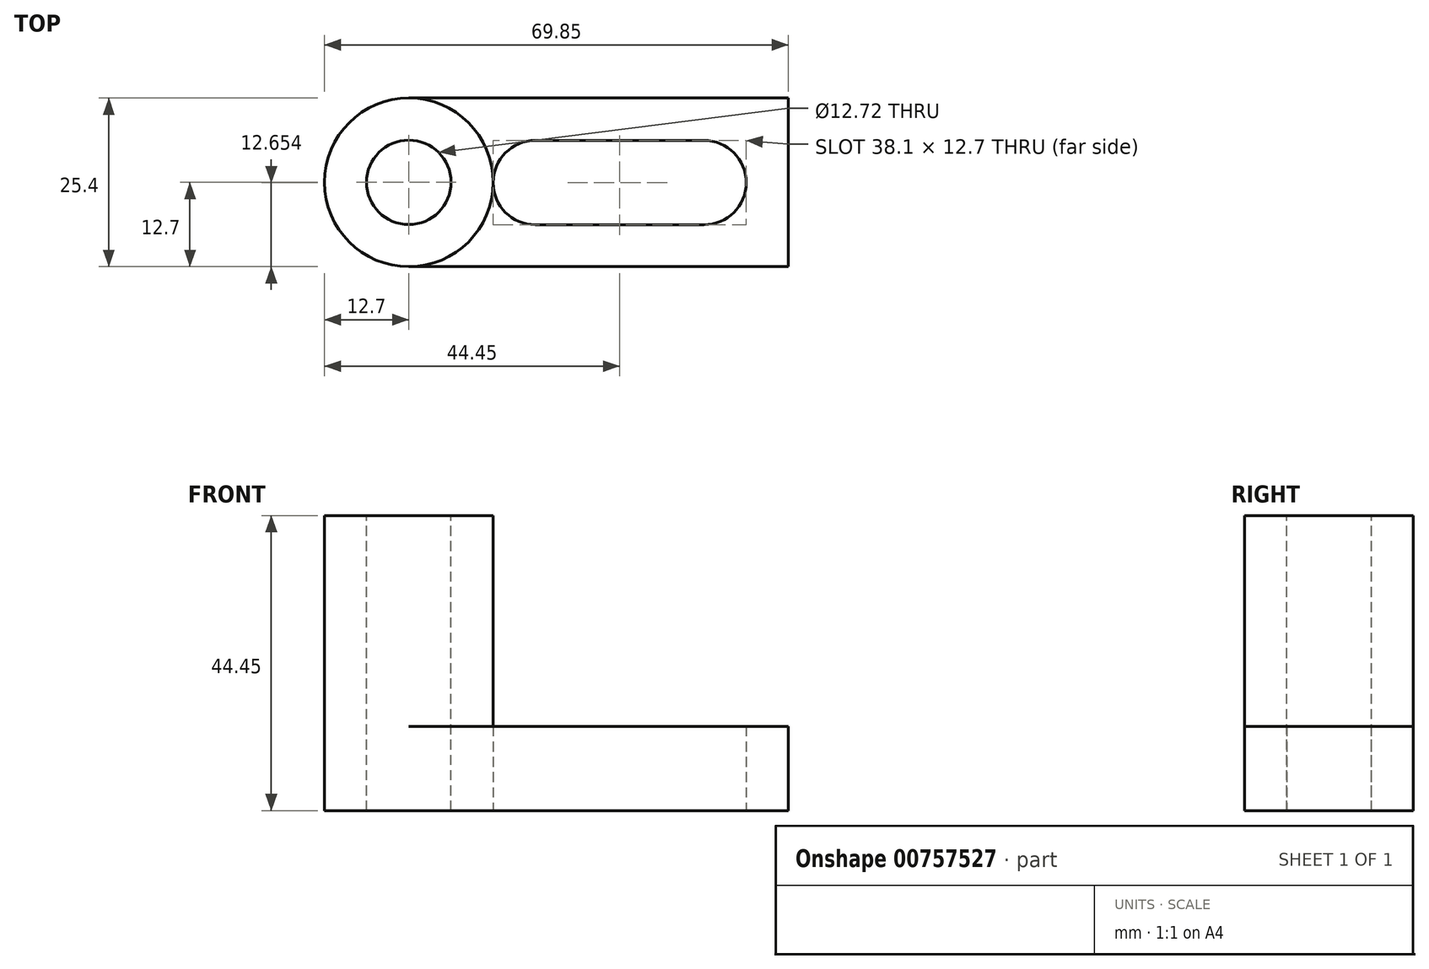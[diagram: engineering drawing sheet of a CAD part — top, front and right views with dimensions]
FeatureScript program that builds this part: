
annotation { "Feature Type Name" : "Feature", "Feature Type Description" : "" }
export const myFeature = defineFeature(function(context is Context, id is Id, definition is map)
    precondition{}
    {
        {
            var Q0;
            Q0=qCreatedBy(makeId("Front.planeOp"),FACE);
            var sketch = newSketch(context, id + "F0", { "sketchPlane" : qUnion([Q0])});
            skLineSegment(sketch, "E0", {"start": v(0, 0) * mm, "end": v(-69.85, 0) * mm});
            skLineSegment(sketch, "E1", {"start": v(-69.85, 0) * mm, "end": v(-69.85, 44.45) * mm});
            skLineSegment(sketch, "E2", {"start": v(-69.85, 44.45) * mm, "end": v(0, 44.45) * mm});
            skLineSegment(sketch, "E3", {"start": v(0, 44.45) * mm, "end": v(0, 0) * mm});
            skSolve(sketch);
        }
        {
            var Q0;
            Q0 = qSketchRegion(id + "F0", true);
            extrude(context, id + "F1", {"entities" : qUnion([Q0]), "depth" : 25.4 * mm, "offsetDistance" : 25.4 * mm});
        }
        {
            var Q0;
            Q0=makeQuery(id+"F1.opExtrude","CAP_FACE",FACE,{"disambiguationData":[OSD([sQuery(id+"F0.wireOp",EDGE,"E0"),sQuery(id+"F0.wireOp",EDGE,"E1"),sQuery(id+"F0.wireOp",EDGE,"E2"),sQuery(id+"F0.wireOp",EDGE,"E3")])],"isStart":false});
            var sketch = newSketch(context, id + "F2", { "sketchPlane" : qUnion([Q0])});
            skLineSegment(sketch, "E4", {"start": v(-44.45, 44.45) * mm, "end": v(-44.45, 12.7) * mm});
            skLineSegment(sketch, "E5", {"start": v(-44.45, 12.7) * mm, "end": v(0, 12.7) * mm});
            skSolve(sketch);
        }
        {
            var Q0;
            {var subQ0=sQuery(id+"F2.wireOp",EDGE,"E4");Q0=makeQuery(id+"F2.imprint","IMPRINT",FACE,{"disambiguationData":[TD([[makeQuery(id+"F2.imprint","IMPRINT",EDGE,{"derivedFrom":subQ0}),1.0]])]});}
            extrude(context, id + "F3", {"entities" : qUnion([Q0]), "operationType" : NewBodyOperationType.REMOVE, "endBound" : BoundingType.THROUGH_ALL, "oppositeDirection" : true, "depth" : 25.4 * mm, "offsetDistance" : 25.4 * mm});
        }
        {
            var Q0;
            Q0=makeQuery(id+"F1.opExtrude","SWEPT_FACE",FACE,{"disambiguationData":[OSD([sQuery(id+"F0.wireOp",EDGE,"E2")])]});
            var sketch = newSketch(context, id + "F4", { "sketchPlane" : qUnion([Q0])});
            skCircle(sketch, "E6", {"center": v(-57.15, -12.7) * mm, "radius": 12.7 * mm});
            skSolve(sketch);
        }
        {
            var Q0;
            {var subQ0=sQuery(id+"F4.wireOp",EDGE,"E6");var subQ1=sQuery(id+"F0.wireOp",EDGE,"E2");var subQ2=makeQuery(id+"F1.opExtrude","CAP_EDGE",EDGE,{"disambiguationData":[OSD([subQ1])],"isStart":true});var subQ3=makeQuery(id+"F4.imprint","INTERSECT",VERTEX,{"derivedFrom":[subQ2,subQ0]});Q0=makeQuery(id+"F4.imprint","IMPRINT",FACE,{"disambiguationData":[TD([[makeQuery(id+"F4.imprint","IMPRINT",EDGE,{"disambiguationData":[TD([[subQ3,-1.0]])],"derivedFrom":subQ0}),-1.0]])]});}
            var Q1;
            {var subQ0=sQuery(id+"F4.wireOp",EDGE,"E6");var subQ1=sQuery(id+"F0.wireOp",EDGE,"E2");var subQ4=makeQuery(id+"F1.opExtrude","CAP_EDGE",EDGE,{"disambiguationData":[OSD([subQ1])],"isStart":false});var subQ5=makeQuery(id+"F4.imprint","INTERSECT",VERTEX,{"derivedFrom":[subQ4,subQ0]});Q1=makeQuery(id+"F4.imprint","IMPRINT",FACE,{"disambiguationData":[TD([[makeQuery(id+"F4.imprint","IMPRINT",EDGE,{"disambiguationData":[TD([[subQ5,1.0]])],"derivedFrom":subQ0}),-1.0]])]});}
            extrude(context, id + "F5", {"entities" : qUnion([Q0, Q1]), "operationType" : NewBodyOperationType.REMOVE, "endBound" : BoundingType.THROUGH_ALL, "oppositeDirection" : true, "depth" : 25.4 * mm, "offsetDistance" : 25.4 * mm});
        }
        {
            var Q0;
            Q0=makeQuery(id+"F1.opExtrude","SWEPT_FACE",FACE,{"disambiguationData":[OSD([sQuery(id+"F0.wireOp",EDGE,"E2")])]});
            var sketch = newSketch(context, id + "F6", { "sketchPlane" : qUnion([Q0])});
            skCircle(sketch, "E7", {"center": v(-57.15, -12.7) * mm, "radius": 12.7 * mm});
            skSolve(sketch);
        }
        {
            var Q0;
            {var subQ1=sQuery(id+"F0.wireOp",EDGE,"E2");var subQ2=makeQuery(id+"F1.opExtrude","CAP_EDGE",EDGE,{"disambiguationData":[OSD([subQ1])],"isStart":true});Q0=makeQuery(id+"F6.imprint","IMPRINT",FACE,{"disambiguationData":[TD([[makeQuery(id+"F6.imprint","IMPRINT",EDGE,{"derivedFrom":subQ2}),-1.0]])]});}
            var Q1;
            {var subQ1=sQuery(id+"F0.wireOp",EDGE,"E2");var subQ2=makeQuery(id+"F1.opExtrude","CAP_EDGE",EDGE,{"disambiguationData":[OSD([subQ1])],"isStart":false});Q1=makeQuery(id+"F6.imprint","IMPRINT",FACE,{"disambiguationData":[TD([[makeQuery(id+"F6.imprint","IMPRINT",EDGE,{"derivedFrom":subQ2}),1.0]])]});}
            extrude(context, id + "F7", {"entities" : qUnion([Q0, Q1]), "operationType" : NewBodyOperationType.REMOVE, "oppositeDirection" : true, "depth" : 31.75 * mm, "offsetDistance" : 25.4 * mm});
        }
        {
            var Q0;
            Q0=makeQuery(id+"F1.opExtrude","SWEPT_FACE",FACE,{"disambiguationData":[OSD([sQuery(id+"F0.wireOp",EDGE,"E0")])]});
            var sketch = newSketch(context, id + "F8", { "sketchPlane" : qUnion([Q0])});
            skLineSegment(sketch, "E8", {"start": v(-6.35, 12.75) * mm, "end": v(-6.35, 12.75) * mm});
            skLineSegment(sketch, "E9", {"start": v(-12.7, 6.4) * mm, "end": v(-38.1, 6.4) * mm});
            skLineSegment(sketch, "E10", {"start": v(-44.45, 12.75) * mm, "end": v(-44.45, 12.75) * mm});
            skLineSegment(sketch, "E11", {"start": v(-38.1, 19.1) * mm, "end": v(-12.7, 19.1) * mm});
            skPoint(sketch, "E12.visualSharp", {"position": v(-44.45, 19.1) * mm});
            skArc(sketch, "E12.filletArc", {"start": v(-38.1, 19.1) * mm, "mid": v(-42.6, 17.24) * mm, "end": v(-44.45, 12.75) * mm});
            skPoint(sketch, "E13.visualSharp", {"position": v(-44.45, 6.4) * mm});
            skArc(sketch, "E13.filletArc", {"start": v(-44.45, 12.75) * mm, "mid": v(-42.6, 8.26) * mm, "end": v(-38.1, 6.4) * mm});
            skPoint(sketch, "E14.visualSharp", {"position": v(-6.35, 19.1) * mm});
            skArc(sketch, "E14.filletArc", {"start": v(-6.35, 12.75) * mm, "mid": v(-8.2, 17.24) * mm, "end": v(-12.7, 19.1) * mm});
            skPoint(sketch, "E15.visualSharp", {"position": v(-6.35, 6.4) * mm});
            skArc(sketch, "E15.filletArc", {"start": v(-12.7, 6.4) * mm, "mid": v(-8.2, 8.26) * mm, "end": v(-6.35, 12.75) * mm});
            skSolve(sketch);
        }
        {
            var Q0;
            Q0=makeQuery(id+"F8.imprint","IMPRINT",FACE,{"disambiguationData":[TD([[makeQuery(id+"F8.imprint","IMPRINT",EDGE,{"derivedFrom":sQuery(id+"F8.wireOp",EDGE,"E9")}),-1.0]])]});
            extrude(context, id + "F9", {"entities" : qUnion([Q0]), "operationType" : NewBodyOperationType.REMOVE, "endBound" : BoundingType.THROUGH_ALL, "oppositeDirection" : true, "depth" : 25.4 * mm, "offsetDistance" : 25.4 * mm});
        }
        {
            var Q0;
            Q0=makeQuery(id+"F1.opExtrude","SWEPT_FACE",FACE,{"disambiguationData":[OSD([sQuery(id+"F0.wireOp",EDGE,"E2")])]});
            var sketch = newSketch(context, id + "F10", { "sketchPlane" : qUnion([Q0])});
            skCircle(sketch, "E16", {"center": v(-57.15, -12.7) * mm, "radius": 6.36 * mm});
            skSolve(sketch);
        }
        {
            var Q0;
            Q0=makeQuery(id+"F10.imprint","IMPRINT",FACE,{"disambiguationData":[TD([[makeQuery(id+"F10.imprint","IMPRINT",EDGE,{"derivedFrom":sQuery(id+"F10.wireOp",EDGE,"E16")}),1.0]])]});
            extrude(context, id + "F11", {"entities" : qUnion([Q0]), "operationType" : NewBodyOperationType.REMOVE, "endBound" : BoundingType.THROUGH_ALL, "oppositeDirection" : true, "depth" : 25.4 * mm, "offsetDistance" : 25.4 * mm});
        }
    });
